# Revit family: Rise 120 Degree Workstation 600 Deep
name_source: partatom
category: Furniture
units: mm (PartAtom-declared; Revit-internal decimal feet)

## family parameters
Always vertical = Yes
Cut with Voids When Loaded = No
OmniClass Number = 23.40.20.00
OmniClass Title = General Furniture and Specialties
Room Calculation Point = No
Shared = No
Work Plane-Based = No

## types (2) — shared parameters
Assembly Code = E2020200
Bung = Gresham - MIDNIGHT ASH
Desktop = Gresham - MIDNIGHT ASH
Foot = Gresham - Black Plastic
Frame = Gresham - Silver Metal
Manufacturer = Gresham Office Furniture
Modesty Panel = Gresham - White MFC
Range = RISE
URL = www.gof.co.uk

## per-type parameters (varying)
| type | Cable Tray Code | Product Code | Width |
| 1000 x 600 x 600 x 1000 | MECT10 | HDY106Z | 1000 mm  [stored 3.28084 ft] |
| 1200 x 600 x 600 x 1200 | MECT12 | HDY126Z | 1200 mm |

note: [stored X ft] marks values corroborated as IEEE doubles in the binary element streams (Revit-internal decimal feet)

## geometry (parser evidence)
native form markers: Sweep x17
no freeform markers — native parametric forms only
